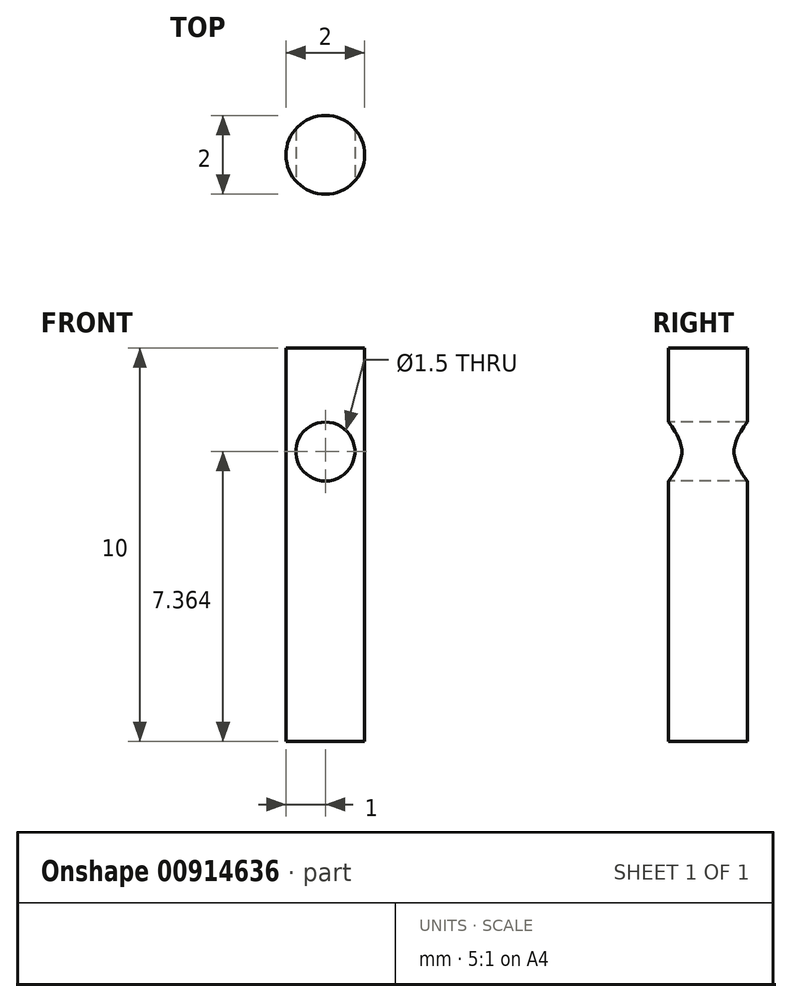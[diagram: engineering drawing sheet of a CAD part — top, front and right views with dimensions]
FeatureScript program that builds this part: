
annotation { "Feature Type Name" : "Feature", "Feature Type Description" : "" }
export const myFeature = defineFeature(function(context is Context, id is Id, definition is map)
    precondition{}
    {
        {
            var Q0;
            Q0=qCreatedBy(makeId("Front.planeOp"),FACE);
            var sketch = newSketch(context, id + "F0", { "sketchPlane" : qUnion([Q0])});
            skLineSegment(sketch, "E0", {"start": v(0, 0) * mm, "end": v(0, 10) * mm});
            skLineSegment(sketch, "E1", {"start": v(-1, 0) * mm, "end": v(-1, 10) * mm});
            skLineSegment(sketch, "E2", {"start": v(-1, 10) * mm, "end": v(0, 10) * mm});
            skLineSegment(sketch, "E3", {"start": v(-1, 0) * mm, "end": v(0, 0) * mm});
            skSolve(sketch);
        }
        {
            var Q0;
            Q0=qSketchRegion(id+"F0",true);
            var Q1;
            Q1=sQuery(id+"F0.wireOp",EDGE,"E1");
            revolve(context, id + "F1", {"surfaceOperationType" : NewSurfaceOperationType.NEW, "entities" : qUnion([Q0]), "axis" : qUnion([Q1]), "revolveType" : RevolveType.FULL});
        }
        {
            var Q0;
            Q0=qCreatedBy(makeId("Front.planeOp"),FACE);
            var sketch = newSketch(context, id + "F2", { "sketchPlane" : qUnion([Q0])});
            skCircle(sketch, "E4", {"center": v(-1, 7.36) * mm, "radius": 0.75 * mm});
            skLineSegment(sketch, "E5", {"start": v(-2, 7.81) * mm, "end": v(-2, 6.18) * mm, "construction": true});
            skLineSegment(sketch, "E6", {"start": v(0, 6.18) * mm, "end": v(0, 7.81) * mm, "construction": true});
            skSolve(sketch);
        }
        {
            var Q0;
            Q0=qSketchRegion(id+"F2",true);
            extrude(context, id + "F3", {"entities" : qUnion([Q0]), "operationType" : NewBodyOperationType.REMOVE, "oppositeDirection" : true, "depth" : 250 * mm, "offsetDistance" : 25 * mm});
        }
        {
            var Q0;
            Q0=qSketchRegion(id+"F2",true);
            extrude(context, id + "F4", {"entities" : qUnion([Q0]), "operationType" : NewBodyOperationType.REMOVE, "depth" : 25 * mm, "offsetDistance" : 25 * mm});
        }
    });
